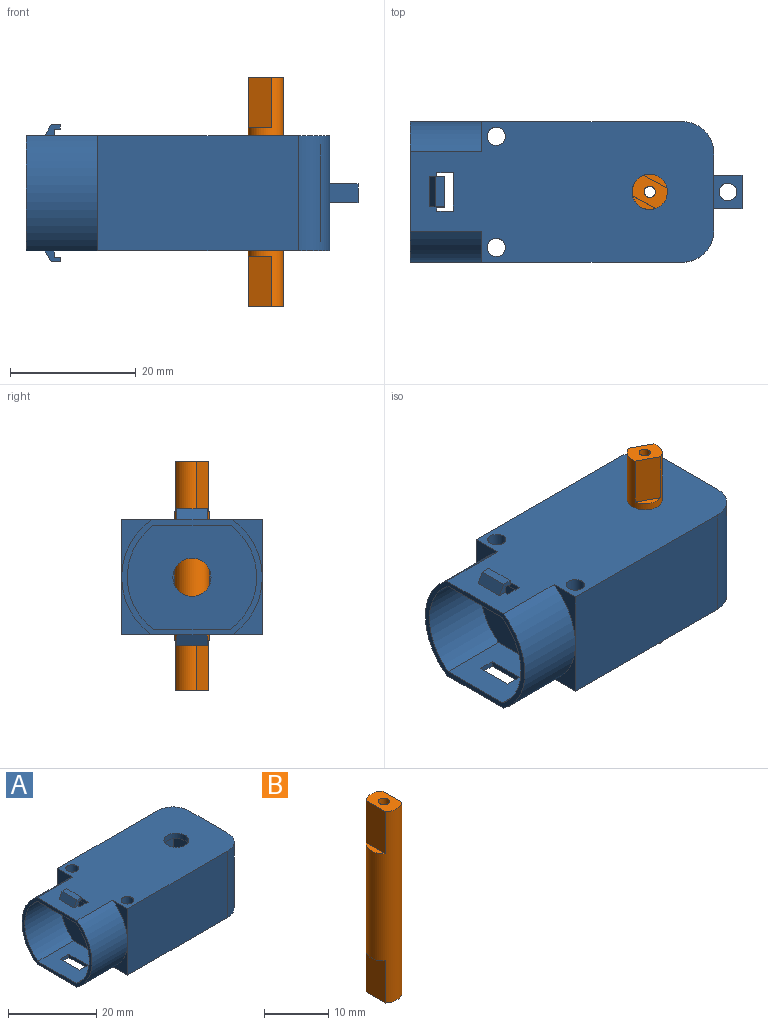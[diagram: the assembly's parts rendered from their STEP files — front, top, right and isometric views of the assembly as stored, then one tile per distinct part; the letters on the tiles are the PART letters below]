
ASSEMBLY  parts=2 mates=1
PART A: 62 faces, bbox 52.9x22.4x21.9 mm
  f0: cylinder r=2.8mm len=5.6mm, axis (0,0,-1), area 26.4mm2, adj f2,f13
  f1: cylinder r=2.8mm len=5.6mm, axis (0,0,-1), area 26.4mm2, adj f3,f12
  f2: plane 48.4x22.4mm, normal (0,0,-1), area 904.1mm2, adj f0,f4,f15,f16,f21,f22,f23,f24
  f3: plane 48.4x22.4mm, normal (0,0,1), area 904.1mm2, adj f1,f4,f15,f16,f21,f22,f23,f24
  f4: plane 18.4x12.4mm, normal (1,0,0), area 212mm2, adj f2,f3,f30,f32,f33,f34,f60,f61
  f5: plane 20.62x16.62mm, normal (-1,0,0), area 271.8mm2, adj f14,f17,f18,f19,f20
  f6: plane 15.4x12.05mm, normal (1,0,0), area 156.6mm2, adj f9,f11,f12,f13,f14
  f7: plane 30.33x15.4mm, normal (0,1,0), area 467mm2, adj f8,f11,f12,f13
  f8: plane 19.4x15.4mm, normal (-1,0,0), area 298.8mm2, adj f7,f10,f12,f13
  f9: cylinder r=2.95mm len=15.4mm, axis (0,0,-1), area 97.9mm2, adj f6,f10,f12,f13
  f10: plane 30.33x15.4mm, normal (0,-1,0), area 467mm2, adj f8,f9,f12,f13
  f11: cylinder r=2.95mm len=15.4mm, axis (0,0,-1), area 97.9mm2, adj f6,f7,f12,f13
  f12: plane 34x19.4mm, normal (0,0,-1), area 610mm2, adj f1,f6,f7,f8,f9,f10,f11
  f13: plane 34x19.4mm, normal (0,0,1), area 610mm2, adj f0,f6,f7,f8,f9,f10,f11
  f14: cylinder r=3.04mm len=6.07mm, axis (-1,0,0), area 28.6mm2, adj f5,f6
  f15: cylinder r=11.2mm len=18.4mm, axis (1,0,0), area 246.1mm2, adj f2,f3,f21,f26,f29
  f16: cylinder r=11.2mm len=18.4mm, axis (1,0,0), area 246.1mm2, adj f2,f3,f21,f25,f28
  f17: cylinder r=10.31mm len=16.62mm, axis (1,0,0), area 220.3mm2, adj f5,f18,f20,f21
  f18: plane 12.21x11.4mm, normal (0,0,-1), area 123.3mm2, adj f5,f17,f19,f21,f40,f41,f42,f43
  f19: cylinder r=10.31mm len=16.62mm, axis (1,0,0), area 220.3mm2, adj f5,f18,f20,f21
  f20: plane 12.21x11.4mm, normal (0,0,1), area 123.3mm2, adj f5,f17,f19,f21,f36,f37,f38,f39
  f21: plane 22.4x18.4mm, normal (-1,0,0), area 58.7mm2, adj f2,f3,f15,f16,f17,f18,f19,f20
  f22: cylinder r=1.45mm len=18.4mm, axis (0,0,-1), area 167.6mm2, adj f2,f3
  f23: cylinder r=1.45mm len=18.4mm, axis (0,0,-1), area 167.6mm2, adj f2,f3
  f24: plane 32x18.4mm, normal (0,-1,0), area 588.8mm2, adj f2,f3,f26,f29,f60
  f25: plane 9.2x4.81mm, normal (-1,0,0), area 13.2mm2, adj f3,f16,f27
  f26: plane 9.2x4.81mm, normal (-1,0,0), area 13.2mm2, adj f3,f15,f24
  f27: plane 32x18.4mm, normal (0,1,0), area 588.8mm2, adj f2,f3,f25,f28,f61
  f28: plane 9.2x4.81mm, normal (-1,0,0), area 13.2mm2, adj f2,f16,f27
  f29: plane 9.2x4.81mm, normal (-1,0,0), area 13.2mm2, adj f2,f15,f24
  f30: plane 4.5x3mm, normal (0,-1,0), area 13.5mm2, adj f4,f31,f33,f34
  f31: plane 5.4x3mm, normal (1,0,0), area 16.2mm2, adj f30,f32,f33,f34
  f32: plane 4.5x3mm, normal (0,1,0), area 13.5mm2, adj f4,f31,f33,f34
  f33: plane 5.4x4.5mm, normal (0,0,1), area 18.1mm2, adj f4,f30,f31,f32,f35
  f34: plane 5.4x4.5mm, normal (0,0,-1), area 18.1mm2, adj f4,f30,f31,f32,f35
  f35: cylinder r=1.4mm len=3mm, axis (0,0,1), area 26.4mm2, adj f33,f34
  f36: plane 2.6x0.89mm, normal (0,-1,0), area 2.3mm2, adj f2,f20,f37,f39
  f37: plane 6.1x0.89mm, normal (-1,0,0), area 5.4mm2, adj f2,f20,f36,f38
  f38: plane 2.6x0.89mm, normal (0,1,0), area 2.3mm2, adj f2,f20,f37,f39
  f39: plane 6.1x0.89mm, normal (1,0,0), area 5.4mm2, adj f2,f20,f36,f38,f52
  f40: plane 6.1x0.89mm, normal (1,0,0), area 5.4mm2, adj f3,f18,f41,f43,f47
  f41: plane 2.6x0.89mm, normal (0,1,0), area 2.3mm2, adj f3,f18,f40,f42
  f42: plane 6.1x0.89mm, normal (-1,0,0), area 5.4mm2, adj f3,f18,f41,f43
  f43: plane 2.6x0.89mm, normal (0,-1,0), area 2.3mm2, adj f3,f18,f40,f42
  f44: plane 4.8x0.75mm, normal (1,0,0), area 3.6mm2, adj f45,f49,f50,f51
  f45: plane 4.8x1.49mm, normal (0,0,1), area 7.1mm2, adj f44,f46,f50,f51
  f46: plane 4.8x1.75mm, normal (-0.88,0,0.48), area 9.6mm2, adj f3,f45,f50,f51
  f47: plane 4.8x0.21mm, normal (0,0,-1), area 1mm2, adj f40,f48,f50,f51
  f48: plane 4.8x1mm, normal (1,0,0), area 4.8mm2, adj f47,f49,f50,f51
  f49: plane 4.8x0.99mm, normal (0,0,-1), area 4.7mm2, adj f44,f48,f50,f51
  f50: plane 2.44x1.75mm, normal (0,-1,0), area 2.4mm2, adj f3,f44,f45,f46,f47,f48,f49
  f51: plane 2.44x1.75mm, normal (0,1,0), area 2.4mm2, adj f3,f44,f45,f46,f47,f48,f49
  f52: plane 4.8x0.21mm, normal (0,0,1), area 1mm2, adj f39,f56,f58,f59
  f53: plane 4.8x0.75mm, normal (1,0,0), area 3.6mm2, adj f54,f57,f58,f59
  f54: plane 4.8x1.49mm, normal (0,0,-1), area 7.1mm2, adj f53,f55,f58,f59
  f55: plane 4.8x1.75mm, normal (-0.88,0,-0.48), area 9.6mm2, adj f2,f54,f58,f59
  f56: plane 4.8x1mm, normal (1,0,0), area 4.8mm2, adj f52,f57,f58,f59
  f57: plane 4.8x0.99mm, normal (0,0,1), area 4.7mm2, adj f53,f56,f58,f59
  f58: plane 2.44x1.75mm, normal (0,-1,0), area 2.4mm2, adj f2,f52,f53,f54,f55,f56,f57
  f59: plane 2.44x1.75mm, normal (0,1,0), area 2.4mm2, adj f2,f52,f53,f54,f55,f56,f57
  f60: cylinder r=5mm len=18.4mm, axis (0,0,1), area 144.5mm2, adj f2,f3,f4,f24
  f61: cylinder r=5mm len=18.4mm, axis (0,0,-1), area 144.5mm2, adj f2,f3,f4,f27
PART B: 12 faces, bbox 5.6x5.6x36.4 mm
  f0: plane 8x4.2mm, normal (-1,0,0), area 33.6mm2, adj f3,f4,f5
  f1: plane 8x4.2mm, normal (1,0,0), area 33.6mm2, adj f3,f4,f6
  f2: cylinder r=0.9mm len=36.4mm, axis (0,0,-1), area 205.8mm2, adj f4,f9
  f3: cylinder r=2.8mm len=36.4mm, axis (0,0,-1), area 488.2mm2, adj f0,f1,f4,f5,f6,f7,f8,f9
  f4: plane 5.6x3.7mm, normal (0,0,1), area 16.5mm2, adj f0,f1,f2,f3
  f5: plane 4.2x0.95mm, normal (0,0,1), area 2.8mm2, adj f0,f3
  f6: plane 4.2x0.95mm, normal (0,0,1), area 2.8mm2, adj f1,f3
  f7: plane 8x4.2mm, normal (-1,0,0), area 33.6mm2, adj f3,f9,f10
  f8: plane 8x4.2mm, normal (1,0,0), area 33.6mm2, adj f3,f9,f11
  f9: plane 5.6x3.7mm, normal (0,0,-1), area 16.5mm2, adj f2,f3,f7,f8
  f10: plane 4.2x0.95mm, normal (0,0,-1), area 2.8mm2, adj f3,f7
  f11: plane 4.2x0.95mm, normal (0,0,-1), area 2.8mm2, adj f3,f8
PLACE A t=(4.14,-0.46,-0.12)mm fixed
PLACE B rot(axis=(0,0,-1),118.1deg) t=(16.36,6.86,0.08)mm
MATE revolute B.f2 <-> A.f0  axis (0,0,-1) through (12.44,-0.46,0.08)mm
